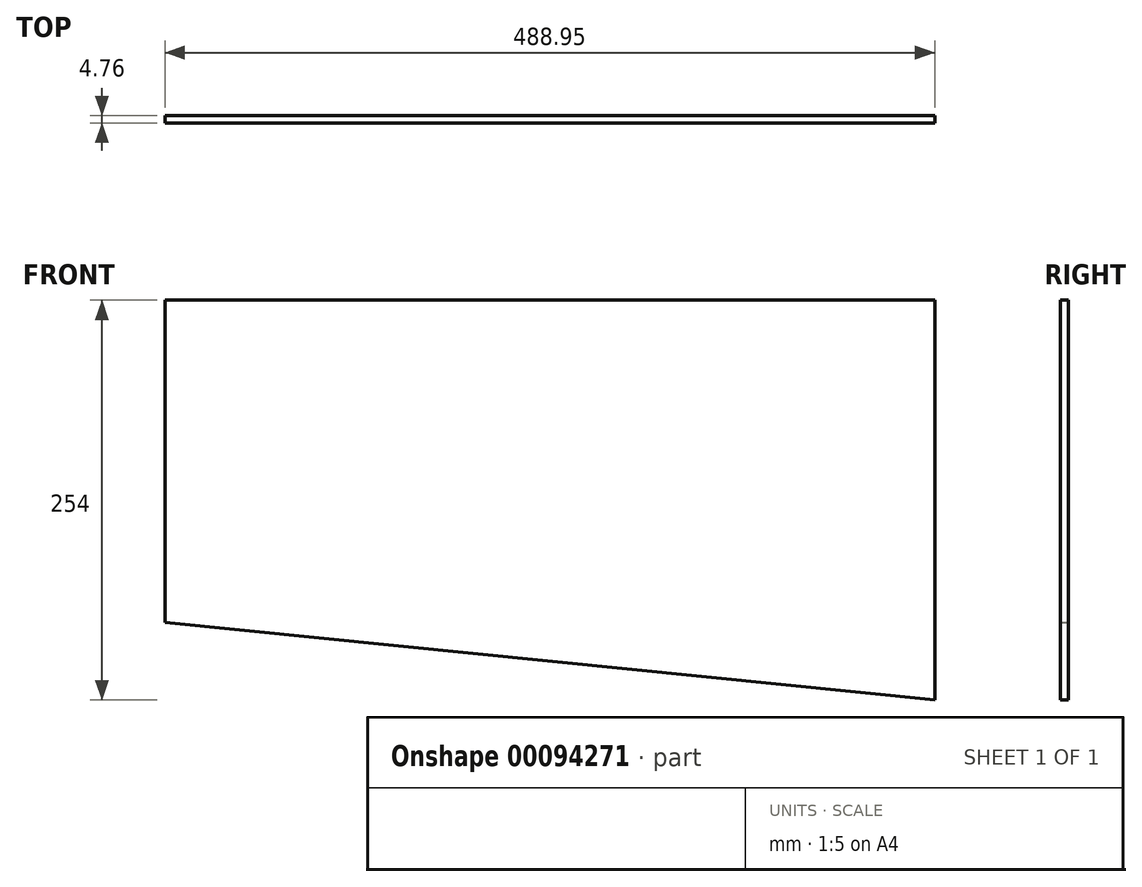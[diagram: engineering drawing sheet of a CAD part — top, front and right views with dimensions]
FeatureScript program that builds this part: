
annotation { "Feature Type Name" : "Feature", "Feature Type Description" : "" }
export const myFeature = defineFeature(function(context is Context, id is Id, definition is map)
    precondition{}
    {
        {
            var Q0;
            Q0=qCreatedBy(makeId("Front.planeOp"),FACE);
            var sketch = newSketch(context, id + "F0", { "sketchPlane" : qUnion([Q0])});
            skLineSegment(sketch, "E0.top", {"start": v(0, 254) * mm, "end": v(-473.08, 254) * mm});
            skLineSegment(sketch, "E0.left", {"start": v(0, 0) * mm, "end": v(0, 254) * mm});
            skLineSegment(sketch, "E1", {"start": v(-473.08, 254) * mm, "end": v(-504.83, 254) * mm});
            skLineSegment(sketch, "E2", {"start": v(-504.83, 50.8) * mm, "end": v(0, 0) * mm});
            skLineSegment(sketch, "E3", {"start": v(-488.95, 254) * mm, "end": v(-488.95, 49.2) * mm});
            skSolve(sketch);
        }
        {
            var Q0;
            Q0 = qSketchRegion(id + "F0", true);
            extrude(context, id + "F1", {"entities" : qUnion([Q0]), "depth" : 4.76 * mm});
        }
    });
